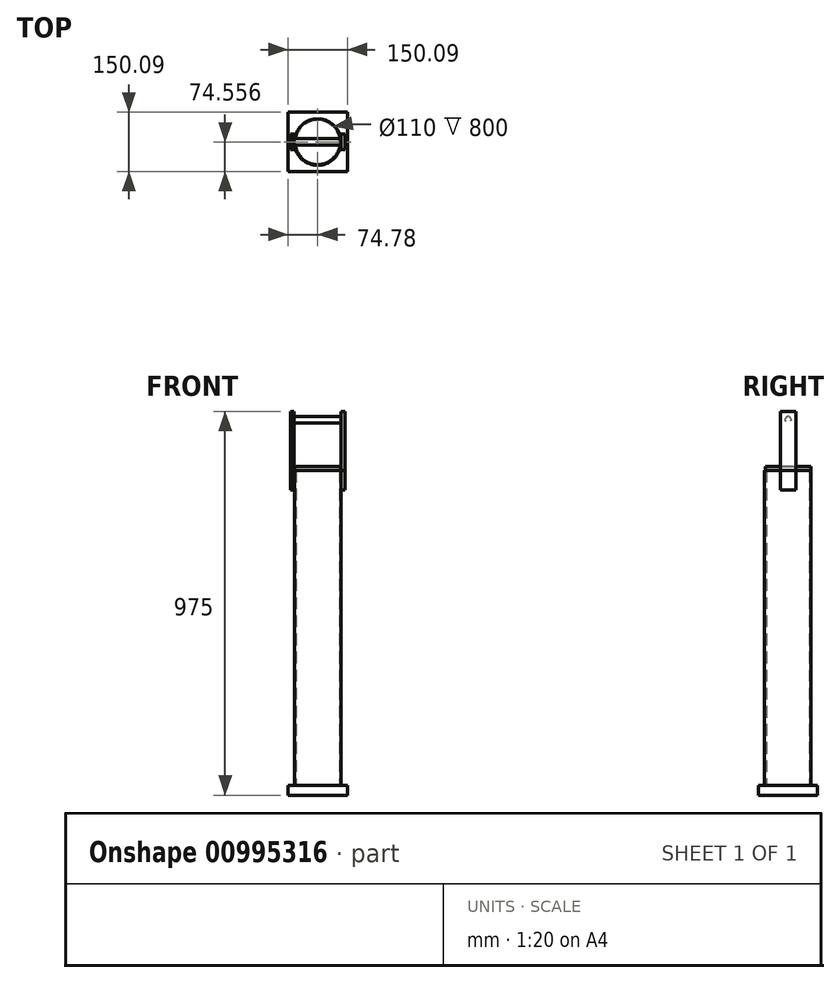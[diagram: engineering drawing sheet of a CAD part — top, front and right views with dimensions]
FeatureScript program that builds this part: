
annotation { "Feature Type Name" : "Feature", "Feature Type Description" : "" }
export const myFeature = defineFeature(function(context is Context, id is Id, definition is map)
    precondition{}
    {
        {
            var Q0;
            Q0=qCreatedBy(makeId("Top.planeOp"),FACE);
            var sketch = newSketch(context, id + "F0", { "sketchPlane" : qUnion([Q0])});
            skCircle(sketch, "E0", {"center": v(0, -0.62) * mm, "radius": 55 * mm});
            skCircle(sketch, "E1", {"center": v(0, -0.62) * mm, "radius": 59 * mm});
            skSolve(sketch);
        }
        {
            var Q0;
            Q0 = qSketchRegion(id + "F0", true);
            var sketch = newSketch(context, id + "F1", { "sketchPlane" : qUnion([Q0])});
            skSolve(sketch);
        }
        {
            var Q0;
            Q0=makeQuery(id+"F1.imprint","IMPRINT",FACE,{"disambiguationData":[TD([[makeQuery(id+"F1.imprint","IMPRINT",EDGE,{"derivedFrom":makeQuery(id+"F0.imprint","IMPRINT",EDGE,{"derivedFrom":sQuery(id+"F0.wireOp",EDGE,"E0")})}),-1.0]])]});
            extrude(context, id + "F2", {"entities" : qUnion([Q0]), "depth" : 800 * mm, "offsetDistance" : 25 * mm});
        }
        {
            var Q0;
            Q0=makeQuery(id+"F2.opExtrude","CAP_FACE",FACE,{"disambiguationData":[OSD([sQuery(id+"F0.wireOp",EDGE,"E0"),sQuery(id+"F0.wireOp",EDGE,"E1")])],"isStart":false});
            var sketch = newSketch(context, id + "F3", { "sketchPlane" : qUnion([Q0])});
            skSolve(sketch);
        }
        {
            var Q0;
            Q0=makeQuery(id+"F3.imprint","IMPRINT",FACE,{"disambiguationData":[TD([[makeQuery(id+"F3.imprint","IMPRINT",EDGE,{"derivedFrom":makeQuery(id+"F2.opExtrude","CAP_EDGE",EDGE,{"disambiguationData":[OSD([sQuery(id+"F0.wireOp",EDGE,"E0")])],"isStart":false})}),-1.0]])]});
            var sketch = newSketch(context, id + "F4", { "sketchPlane" : qUnion([Q0])});
            skLineSegment(sketch, "E2", {"start": v(59.48, 0) * mm, "end": v(59.48, 20) * mm});
            skLineSegment(sketch, "E3", {"start": v(59.48, 20) * mm, "end": v(69.48, 20) * mm});
            skLineSegment(sketch, "E4", {"start": v(69.48, 20) * mm, "end": v(69.48, -20) * mm});
            skLineSegment(sketch, "E5", {"start": v(69.48, -20) * mm, "end": v(59.48, -20) * mm});
            skLineSegment(sketch, "E6", {"start": v(59.48, -20) * mm, "end": v(59.48, 0) * mm});
            skLineSegment(sketch, "E7.MirrorCS", {"start": v(-59.48, 0) * mm, "end": v(-59.48, 20) * mm});
            skLineSegment(sketch, "E8.MirrorCS", {"start": v(-59.48, 20) * mm, "end": v(-69.48, 20) * mm});
            skLineSegment(sketch, "E9.MirrorCS", {"start": v(-59.48, -20) * mm, "end": v(-59.48, 0) * mm});
            skLineSegment(sketch, "E10.MirrorCS", {"start": v(-69.48, -20) * mm, "end": v(-59.48, -20) * mm});
            skLineSegment(sketch, "E11.MirrorCS", {"start": v(-69.48, 20) * mm, "end": v(-69.48, -20) * mm});
            skSolve(sketch);
        }
        {
            var Q0;
            Q0 = qSketchRegion(id + "F4", true);
            extrude(context, id + "F5", {"entities" : qUnion([Q0]), "depth" : 150 * mm, "offsetDistance" : 25 * mm});
        }
        {
            var Q0;
            Q0=makeQuery(id+"F5.opExtrude","SWEPT_FACE",FACE,{"disambiguationData":[OSD([sQuery(id+"F4.wireOp",EDGE,"E11.MirrorCS")])]});
            var sketch = newSketch(context, id + "F6", { "sketchPlane" : qUnion([Q0])});
            skCircle(sketch, "E12", {"center": v(0, 928.93) * mm, "radius": 7.88 * mm});
            skPoint(sketch, "E12.centerSnap0", {"position": v(0, 950) * mm});
            skSolve(sketch);
        }
        {
            var Q0;
            Q0 = qSketchRegion(id + "F6", true);
            extrude(context, id + "F7", {"entities" : qUnion([Q0]), "oppositeDirection" : true, "depth" : 130 * mm, "offsetDistance" : 25 * mm});
        }
        {
            var Q0;
            Q0=qCreatedBy(makeId("Top.planeOp"),FACE);
            var sketch = newSketch(context, id + "F8", { "sketchPlane" : qUnion([Q0])});
            skLineSegment(sketch, "E13.bottom", {"start": v(-74.78, -75.18) * mm, "end": v(75.3, -75.18) * mm});
            skLineSegment(sketch, "E13.top", {"start": v(-74.78, 74.9) * mm, "end": v(75.3, 74.9) * mm});
            skLineSegment(sketch, "E13.left", {"start": v(-74.78, -75.18) * mm, "end": v(-74.78, 74.9) * mm});
            skLineSegment(sketch, "E13.right", {"start": v(75.3, -75.18) * mm, "end": v(75.3, 74.9) * mm});
            skSolve(sketch);
        }
        {
            var Q0;
            Q0 = qSketchRegion(id + "F8", true);
            extrude(context, id + "F9", {"entities" : qUnion([Q0]), "operationType" : NewBodyOperationType.ADD, "oppositeDirection" : true, "depth" : 25 * mm, "offsetDistance" : 25 * mm});
        }
        {
            var Q0;
            Q0=makeQuery(id+"F3.imprint","IMPRINT",FACE,{"disambiguationData":[TD([[makeQuery(id+"F3.imprint","IMPRINT",EDGE,{"derivedFrom":makeQuery(id+"F2.opExtrude","CAP_EDGE",EDGE,{"disambiguationData":[OSD([sQuery(id+"F0.wireOp",EDGE,"E0")])],"isStart":false})}),-1.0]])]});
            var sketch = newSketch(context, id + "F10", { "sketchPlane" : qUnion([Q0])});
            skCircle(sketch, "E14", {"center": v(0, 0) * mm, "radius": 58.15 * mm});
            skSolve(sketch);
        }
        {
            var Q0;
            Q0 = qSketchRegion(id + "F10", true);
            extrude(context, id + "F11", {"entities" : qUnion([Q0]), "operationType" : NewBodyOperationType.ADD, "depth" : 10 * mm, "offsetDistance" : 25 * mm});
        }
        {
            var Q0;
            Q0=makeQuery(id+"F5.opExtrude","CAP_FACE",FACE,{"disambiguationData":[OSD([sQuery(id+"F4.wireOp",EDGE,"E7.MirrorCS"),sQuery(id+"F4.wireOp",EDGE,"E8.MirrorCS"),sQuery(id+"F4.wireOp",EDGE,"E9.MirrorCS"),sQuery(id+"F4.wireOp",EDGE,"E10.MirrorCS"),sQuery(id+"F4.wireOp",EDGE,"E11.MirrorCS")])],"isStart":true});
            var sketch = newSketch(context, id + "F12", { "sketchPlane" : qUnion([Q0])});
            skLineSegment(sketch, "E15.bottom", {"start": v(-69.48, 20) * mm, "end": v(-59.48, 20) * mm});
            skLineSegment(sketch, "E15.top", {"start": v(-69.48, -20) * mm, "end": v(-59.48, -20) * mm});
            skLineSegment(sketch, "E15.left", {"start": v(-69.48, 20) * mm, "end": v(-69.48, -20) * mm});
            skLineSegment(sketch, "E15.right", {"start": v(-59.48, 20) * mm, "end": v(-59.48, -20) * mm});
            skLineSegment(sketch, "E16.bottom", {"start": v(59.54, -20) * mm, "end": v(69.62, -20) * mm});
            skLineSegment(sketch, "E16.top", {"start": v(59.54, 20) * mm, "end": v(69.62, 20) * mm});
            skLineSegment(sketch, "E16.left", {"start": v(59.54, -20) * mm, "end": v(59.54, 20) * mm});
            skLineSegment(sketch, "E16.right", {"start": v(69.62, -20) * mm, "end": v(69.62, 20) * mm});
            skSolve(sketch);
        }
        {
            var Q0;
            Q0 = qSketchRegion(id + "F12", true);
            extrude(context, id + "F13", {"entities" : qUnion([Q0]), "depth" : 50 * mm, "offsetDistance" : 25 * mm});
        }
    });
